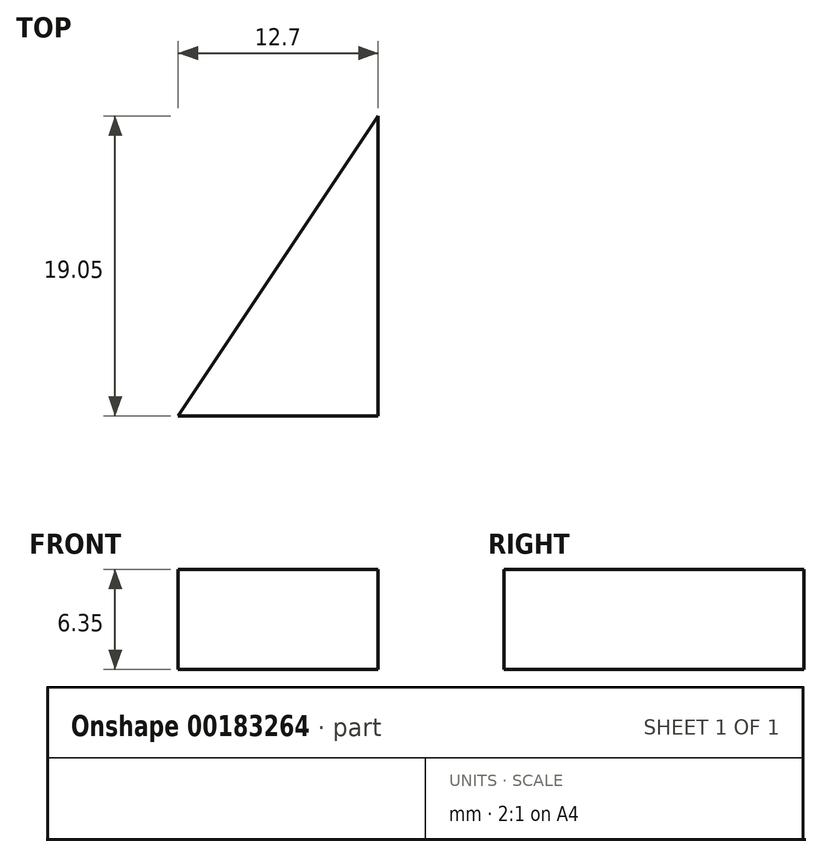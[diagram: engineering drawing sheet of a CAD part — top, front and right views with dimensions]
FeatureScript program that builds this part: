
annotation { "Feature Type Name" : "Feature", "Feature Type Description" : "" }
export const myFeature = defineFeature(function(context is Context, id is Id, definition is map)
    precondition{}
    {
        {
            var Q0;
            Q0=qCreatedBy(makeId("Top.planeOp"),FACE);
            var sketch = newSketch(context, id + "F0", { "sketchPlane" : qUnion([Q0])});
            skLineSegment(sketch, "E0", {"start": v(0, 0) * mm, "end": v(12.7, 0) * mm});
            skLineSegment(sketch, "E1", {"start": v(12.7, 0) * mm, "end": v(12.7, 19.05) * mm});
            skLineSegment(sketch, "E2", {"start": v(12.7, 19.05) * mm, "end": v(0, 0) * mm});
            skSolve(sketch);
        }
        {
            var Q0;
            Q0=makeQuery(id+"F0.imprint","IMPRINT",FACE,{"disambiguationData":[TD([[makeQuery(id+"F0.imprint","IMPRINT",EDGE,{"derivedFrom":sQuery(id+"F0.wireOp",EDGE,"E0")}),1.0]])]});
            extrude(context, id + "F1", {"entities" : qUnion([Q0]), "depth" : 6.35 * mm});
        }
    });
